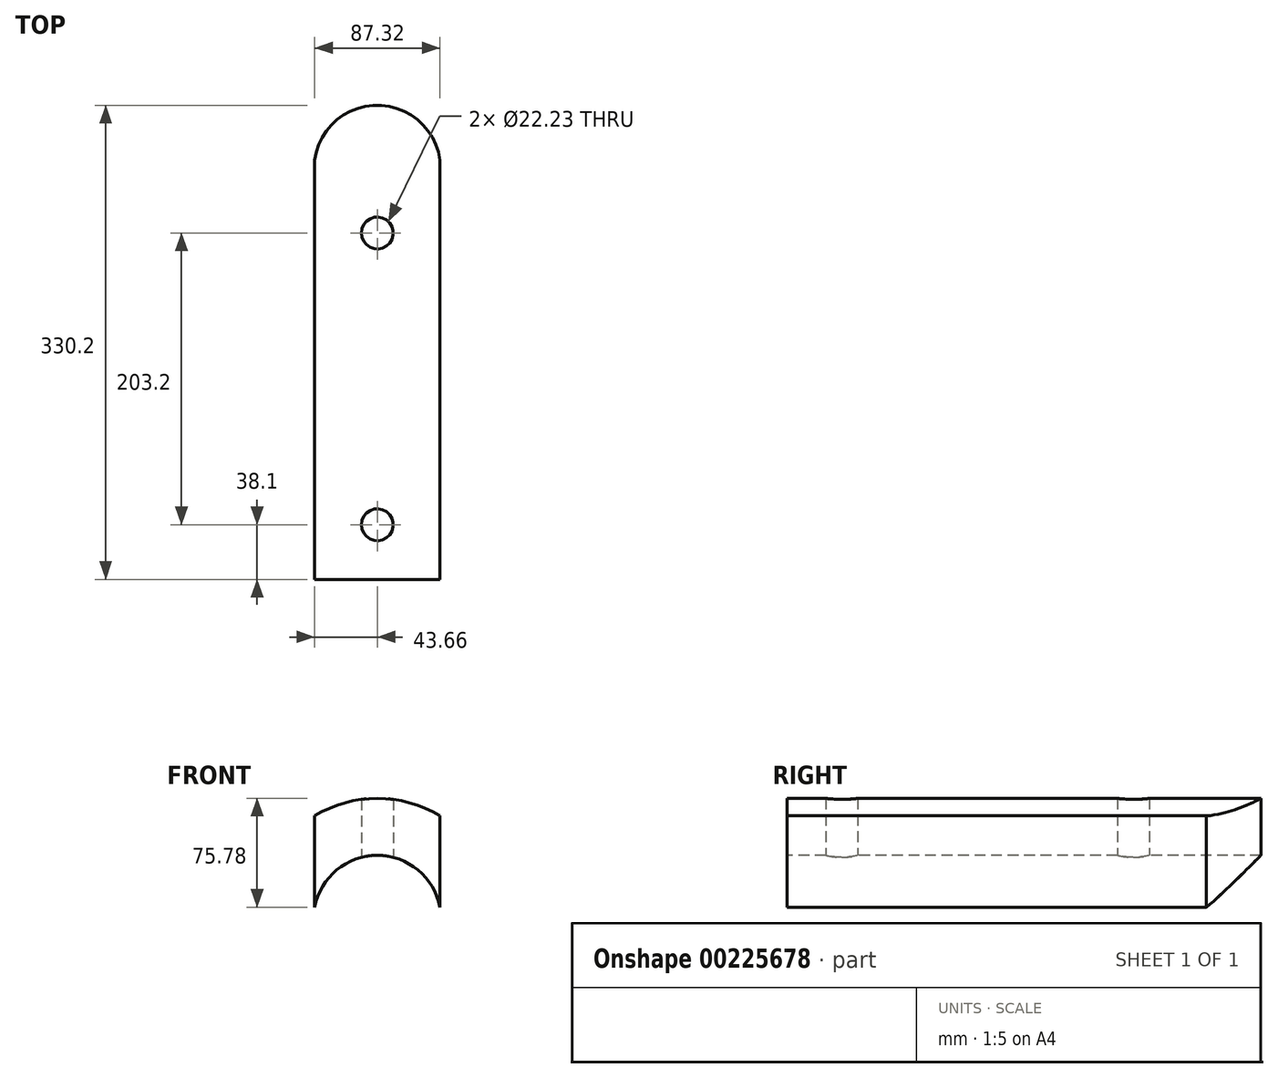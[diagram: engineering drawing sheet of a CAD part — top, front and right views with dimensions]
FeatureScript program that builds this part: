
annotation { "Feature Type Name" : "Feature", "Feature Type Description" : "" }
export const myFeature = defineFeature(function(context is Context, id is Id, definition is map)
    precondition{}
    {
        {
            var Q0;
            Q0=qCreatedBy(makeId("Front.planeOp"),FACE);
            var sketch = newSketch(context, id + "F0", { "sketchPlane" : qUnion([Q0])});
            skArc(sketch, "E0", {"start": v(43.66, 8.36) * mm, "mid": v(0, 44.45) * mm, "end": v(-43.66, 8.36) * mm});
            skArc(sketch, "E1", {"start": v(43.66, 71.93) * mm, "mid": v(0, 84.14) * mm, "end": v(-43.66, 71.93) * mm});
            skLineSegment(sketch, "E2", {"start": v(-43.66, 8.36) * mm, "end": v(-43.66, 71.93) * mm});
            skLineSegment(sketch, "E3", {"start": v(43.66, 8.36) * mm, "end": v(43.66, 71.93) * mm});
            skSolve(sketch);
        }
        {
            var Q0;
            Q0=makeQuery(id+"F0.imprint","IMPRINT",FACE,{"disambiguationData":[TD([[makeQuery(id+"F0.imprint","IMPRINT",EDGE,{"derivedFrom":sQuery(id+"F0.wireOp",EDGE,"E0")}),-1.0]])]});
            extrude(context, id + "F1", {"entities" : qUnion([Q0]), "oppositeDirection" : true, "depth" : 330.2 * mm});
        }
        {
            var Q0;
            Q0=qCreatedBy(makeId("Top.planeOp"),FACE);
            var sketch = newSketch(context, id + "F2", { "sketchPlane" : qUnion([Q0])});
            skLineSegment(sketch, "E4.0.0", {"start": v(-43.66, 0) * mm, "end": v(43.66, 0) * mm});
            skLineSegment(sketch, "E4.0.1", {"start": v(43.66, 0) * mm, "end": v(43.66, 330.2) * mm});
            skLineSegment(sketch, "E4.0.2", {"start": v(43.66, 330.2) * mm, "end": v(0, 330.2) * mm});
            skLineSegment(sketch, "E4.0.3", {"start": v(-43.66, 292.1) * mm, "end": v(-43.66, 0) * mm});
            skLineSegment(sketch, "E5", {"start": v(0, 0) * mm, "end": v(0, 292.1) * mm});
            skLineSegment(sketch, "E6", {"start": v(0, 292.1) * mm, "end": v(43.66, 292.1) * mm});
            skLineSegment(sketch, "E7", {"start": v(0, 292.1) * mm, "end": v(-43.66, 292.1) * mm});
            skArc(sketch, "E8", {"start": v(43.66, 292.1) * mm, "mid": v(28.97, 319.34) * mm, "end": v(0, 330.2) * mm});
            skArc(sketch, "E9", {"start": v(0, 330.2) * mm, "mid": v(-28.97, 319.34) * mm, "end": v(-43.66, 292.1) * mm});
            skLineSegment(sketch, "E10", {"start": v(-43.66, 330.2) * mm, "end": v(0, 330.2) * mm});
            skLineSegment(sketch, "E11", {"start": v(-43.66, 330.2) * mm, "end": v(-43.66, 292.1) * mm});
            skSolve(sketch);
        }
        {
            var Q0;
            Q0=makeQuery(id+"F2.imprint","IMPRINT",FACE,{"disambiguationData":[TD([[makeQuery(id+"F2.imprint","IMPRINT",EDGE,{"derivedFrom":sQuery(id+"F2.wireOp",EDGE,"E9")}),-1.0]])]});
            var Q1;
            {var subQ0=sQuery(id+"F2.wireOp",EDGE,"E4.0.2");Q1=makeQuery(id+"F2.imprint","IMPRINT",FACE,{"disambiguationData":[TD([[makeQuery(id+"F2.imprint","IMPRINT",EDGE,{"derivedFrom":subQ0}),1.0]])]});}
            extrude(context, id + "F3", {"entities" : qUnion([Q0, Q1]), "operationType" : NewBodyOperationType.REMOVE, "endBound" : BoundingType.THROUGH_ALL, "depth" : 25.4 * mm});
        }
        {
            var Q0;
            Q0=qCreatedBy(makeId("Top.planeOp"),FACE);
            var sketch = newSketch(context, id + "F4", { "sketchPlane" : qUnion([Q0])});
            skLineSegment(sketch, "E12", {"start": v(0, 0) * mm, "end": v(0, 38.1) * mm, "construction": true});
            skLineSegment(sketch, "E13", {"start": v(0, 38.1) * mm, "end": v(0, 241.3) * mm, "construction": true});
            skCircle(sketch, "E14", {"center": v(0, 38.1) * mm, "radius": 11.11 * mm});
            skCircle(sketch, "E15", {"center": v(0, 241.3) * mm, "radius": 11.11 * mm});
            skSolve(sketch);
        }
        {
            var Q0;
            Q0=makeQuery(id+"F4.imprint","IMPRINT",FACE,{"disambiguationData":[TD([[makeQuery(id+"F4.imprint","IMPRINT",EDGE,{"derivedFrom":sQuery(id+"F4.wireOp",EDGE,"E15")}),1.0]])]});
            var Q1;
            Q1=makeQuery(id+"F4.imprint","IMPRINT",FACE,{"disambiguationData":[TD([[makeQuery(id+"F4.imprint","IMPRINT",EDGE,{"derivedFrom":sQuery(id+"F4.wireOp",EDGE,"E14")}),1.0]])]});
            extrude(context, id + "F5", {"entities" : qUnion([Q0, Q1]), "operationType" : NewBodyOperationType.REMOVE, "endBound" : BoundingType.THROUGH_ALL, "depth" : 25.4 * mm});
        }
    });
